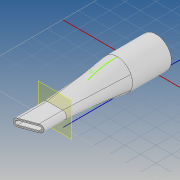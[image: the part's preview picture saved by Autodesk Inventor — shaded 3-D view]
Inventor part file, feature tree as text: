
AUTODESK INVENTOR PART (.ipt)
format: ipt  version: 2021 (Build 250183000, 183)  size: 305,152 bytes
history: native  units: mm
features: sketch x5, projected_geometry x5, extrude x4, other x4, loft x2, plane x1, fillet x1
ambient origin geometry x8: Origin, YZ Plane, XZ Plane, XY Plane, X Axis, Y Axis, Z Axis, Center Point
bodies: Solid1 (feature_tree), Solid3 (feature_tree)
feature tree (22):
  extrude  "Extrusion1"  Depth=80.0mm
  plane  "Work Plane1"
  sketch  "Sketch3"  dims[d5=10.0mm d6=10.0mm]
  extrude  "Extrusion2"  Depth=10.0mm
  sketch  "Sketch7"  dims[d19=2.5mm d22=39.65mm]
  extrude  "Extrusion5"  Depth=50.0mm TaperAngle=0.0deg
  loft  "Loft3"
  loft  "Loft5"
  extrude  "Extrusion6"  TaperAngle=0.0deg  [1 undecoded]
  fillet  "Fillet1"  [1 undecoded]
  sketch  "Sketch2"  dims[d2=50.0mm d3=0.0mm d4=80.0mm]
  projected_geometry  "Projected Loop1"
  sketch  "Sketch4"  dims[d11=34.65mm d12=50.0mm d13=0.0mm]
  projected_geometry  "Projected Loop5"
  other  "Edges4"
  other  "Edges5"
  other  "Edges8"
  other  "Edges9"
  sketch  "Sketch8"  dims[d23=40.0mm d24=0.0mm d33=0.0mm d34=90.0deg d35=0.0mm d36=90.0deg d41=0.0mm d42=90.0deg d43=0.0mm d44=90.0deg d45=3.490659mm d46=10.0mm d47=0.0mm d48=0.5mm]
  projected_geometry  "Projected Loop7"
  projected_geometry  "Projected Loop8"
  projected_geometry  "Projected Loop9"
note: 2 required parameter values undecoded (feature->parameter linkage not recoverable at this tier; creation-order binding heuristic only, values carry confidence <= 0.55)
